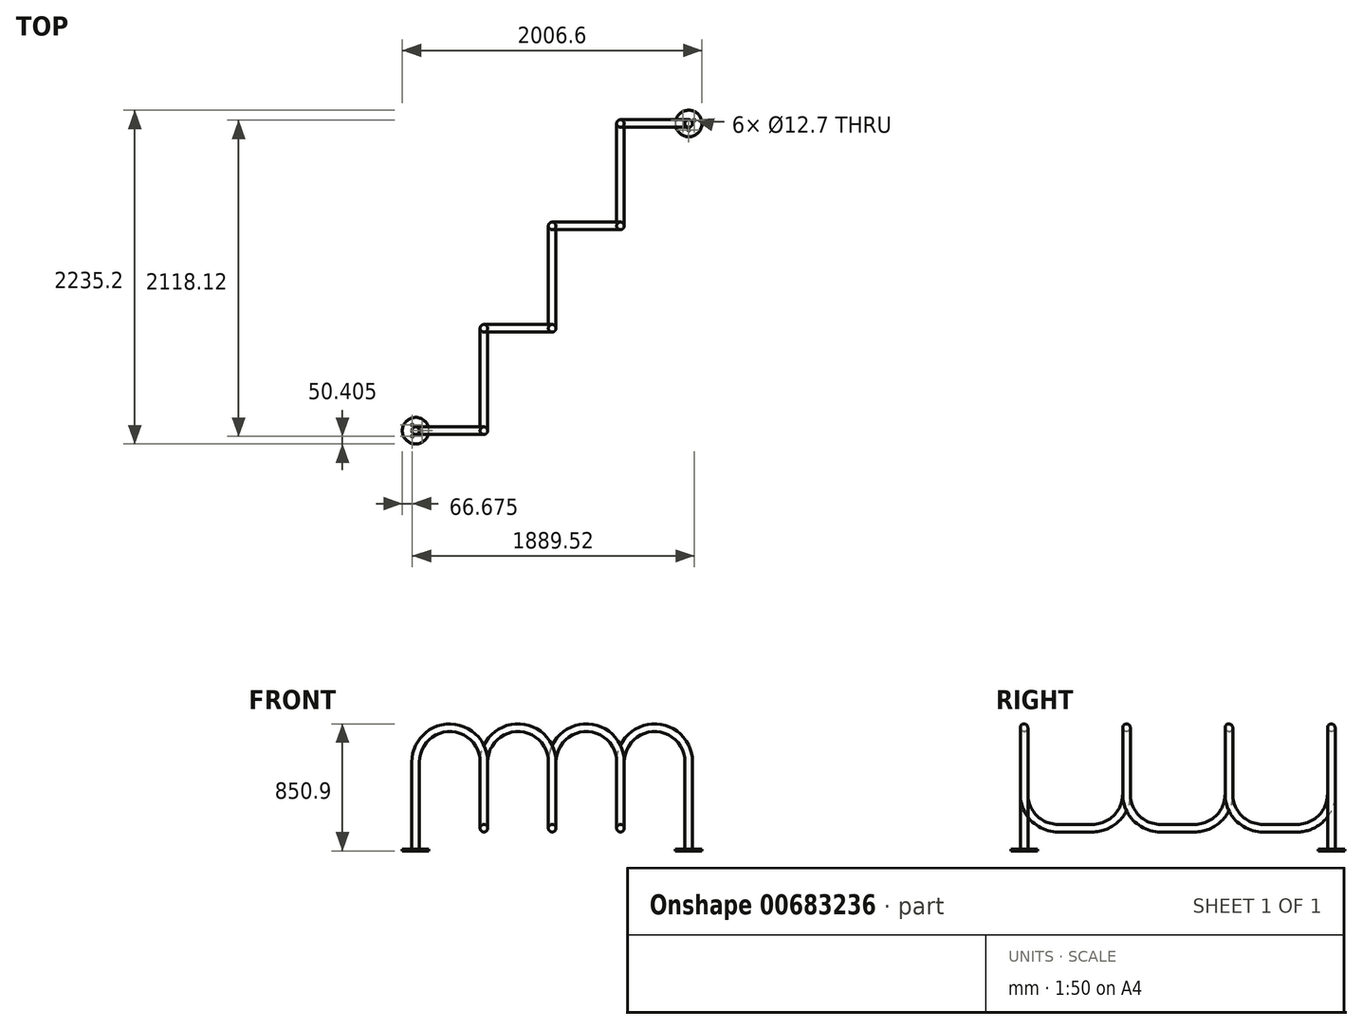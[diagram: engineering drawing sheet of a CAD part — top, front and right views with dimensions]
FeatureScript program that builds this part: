
annotation { "Feature Type Name" : "Feature", "Feature Type Description" : "" }
export const myFeature = defineFeature(function(context is Context, id is Id, definition is map)
    precondition{}
    {
        {
            var Q0;
            Q0=qCreatedBy(makeId("Front.planeOp"),FACE);
            var sketch = newSketch(context, id + "F0", { "sketchPlane" : qUnion([Q0])});
            skLineSegment(sketch, "E0", {"start": v(0, 0) * mm, "end": v(0, 596.9) * mm});
            skArc(sketch, "E1", {"start": v(457.2, 596.9) * mm, "mid": v(228.6, 825.5) * mm, "end": v(0, 596.9) * mm});
            skLineSegment(sketch, "E2", {"start": v(457.2, 596.9) * mm, "end": v(457.2, 381) * mm});
            skSolve(sketch);
        }
        {
            var Q0;
            Q0=sQuery(id+"F0.wireOp",EDGE,"E2");
            cPlane(context, id + "F1", {"entities" : qUnion([Q0]), "cplaneType" : CPlaneType.LINE_ANGLE, "offset" : 25.4 * mm, "angle" : 0 * degree, "width" : 152.4 * mm, "height" : 152.4 * mm});
        }
        {
            var Q0;
            Q0=qCreatedBy(id+"F1.planeOp",FACE);
            var sketch = newSketch(context, id + "F2", { "sketchPlane" : qUnion([Q0])});
            skLineSegment(sketch, "E3", {"start": v(-228.6, 152.4) * mm, "end": v(-457.2, 152.4) * mm});
            skLineSegment(sketch, "E4", {"start": v(-685.8, 381) * mm, "end": v(-685.8, 381) * mm});
            skLineSegment(sketch, "E5", {"start": v(-685.8, 381) * mm, "end": v(-685.8, 596.9) * mm});
            skLineSegment(sketch, "E6.0", {"start": v(0, 596.9) * mm, "end": v(0, 381) * mm});
            skArc(sketch, "E7.filletArc", {"start": v(-228.6, 152.4) * mm, "mid": v(-66.96, 219.36) * mm, "end": v(0, 381) * mm});
            skPoint(sketch, "E8.visualSharp", {"position": v(-685.8, 152.4) * mm});
            skArc(sketch, "E8.filletArc", {"start": v(-685.8, 381) * mm, "mid": v(-618.84, 219.36) * mm, "end": v(-457.2, 152.4) * mm});
            skSolve(sketch);
        }
        {
            var Q0;
            Q0=qCreatedBy(makeId("Top.planeOp"),FACE);
            var sketch = newSketch(context, id + "F3", { "sketchPlane" : qUnion([Q0])});
            skCircle(sketch, "E9", {"center": v(0, 0) * mm, "radius": 25.4 * mm});
            skSolve(sketch);
        }
        {
            var Q0;
            Q0 = qSketchRegion(id + "F3", true);
            var Q1;
            Q1=sQuery(id+"F0.wireOp",EDGE,"E0");
            var Q2;
            Q2=sQuery(id+"F0.wireOp",EDGE,"E1");
            var Q3;
            Q3=sQuery(id+"F2.wireOp",EDGE,"E6.0");
            var Q4;
            Q4=sQuery(id+"F2.wireOp",EDGE,"E7.filletArc");
            var Q5;
            Q5=sQuery(id+"F2.wireOp",EDGE,"E3");
            var Q6;
            Q6=sQuery(id+"F2.wireOp",EDGE,"E8.filletArc");
            var Q7;
            Q7=sQuery(id+"F2.wireOp",EDGE,"E5");
            sweep(context, id + "F4", {"profiles" : qUnion([Q0]), "path" : qUnion([Q1, Q2, Q3, Q4, Q5, Q6, Q7])});
        }
        {
            var Q0;
            Q0=sQuery(id+"F2.wireOp",EDGE,"E5");
            cPlane(context, id + "F5", {"entities" : qUnion([Q0]), "cplaneType" : CPlaneType.LINE_ANGLE, "offset" : 25.4 * mm, "angle" : 90 * degree, "width" : 152.4 * mm, "height" : 152.4 * mm});
        }
        {
            var Q0;
            Q0=qCreatedBy(id+"F5.planeOp",FACE);
            var sketch = newSketch(context, id + "F6", { "sketchPlane" : qUnion([Q0])});
            skArc(sketch, "E10", {"start": v(-457.2, 596.9) * mm, "mid": v(-685.8, 825.5) * mm, "end": v(-914.4, 596.9) * mm});
            skLineSegment(sketch, "E11", {"start": v(-914.4, 596.9) * mm, "end": v(-914.4, 381) * mm});
            skSolve(sketch);
        }
        {
            var Q0;
            Q0=makeQuery(id+"F4.opSweep","CAP_FACE",FACE,{"disambiguationData":[OSD([sQuery(id+"F2.wireOp",VERTEX,"E5.end"),sQuery(id+"F3.wireOp",EDGE,"E9")])],"isStart":false});
            var Q1;
            Q1=sQuery(id+"F6.wireOp",EDGE,"E10");
            var Q2;
            Q2=sQuery(id+"F6.wireOp",EDGE,"E11");
            sweep(context, id + "F7", {"operationType" : NewBodyOperationType.ADD, "profiles" : qUnion([Q0]), "path" : qUnion([Q1, Q2])});
        }
        {
            var Q0;
            Q0=sQuery(id+"F6.wireOp",EDGE,"E11");
            cPlane(context, id + "F8", {"entities" : qUnion([Q0]), "cplaneType" : CPlaneType.LINE_ANGLE, "offset" : 25.4 * mm, "angle" : 0 * degree, "width" : 152.4 * mm, "height" : 152.4 * mm});
        }
        {
            var Q0;
            Q0=qCreatedBy(id+"F8.planeOp",FACE);
            var sketch = newSketch(context, id + "F9", { "sketchPlane" : qUnion([Q0])});
            skPoint(sketch, "E12.0", {"position": v(-685.8, 381) * mm});
            skLineSegment(sketch, "E13", {"start": v(-685.8, 381) * mm, "end": v(-685.8, 381) * mm});
            skLineSegment(sketch, "E14", {"start": v(-914.4, 152.4) * mm, "end": v(-1143, 152.4) * mm});
            skLineSegment(sketch, "E15", {"start": v(-1371.6, 381) * mm, "end": v(-1371.6, 381) * mm});
            skPoint(sketch, "E16.visualSharp", {"position": v(-685.8, 152.4) * mm});
            skArc(sketch, "E16.filletArc", {"start": v(-914.4, 152.4) * mm, "mid": v(-752.76, 219.36) * mm, "end": v(-685.8, 381) * mm});
            skPoint(sketch, "E17.visualSharp", {"position": v(-1371.6, 152.4) * mm});
            skArc(sketch, "E17.filletArc", {"start": v(-1371.6, 381) * mm, "mid": v(-1304.64, 219.36) * mm, "end": v(-1143, 152.4) * mm});
            skLineSegment(sketch, "E18", {"start": v(-1371.6, 381) * mm, "end": v(-1371.6, 596.9) * mm});
            skSolve(sketch);
        }
        {
            var Q0;
            Q0=makeQuery(id+"F7.opSweep","CAP_FACE",FACE,{"disambiguationData":[OSD([sQuery(id+"F2.wireOp",VERTEX,"E5.end"),sQuery(id+"F3.wireOp",EDGE,"E9"),sQuery(id+"F6.wireOp",VERTEX,"E11.end")])],"isStart":false});
            var Q1;
            Q1=sQuery(id+"F9.wireOp",EDGE,"E16.filletArc");
            var Q2;
            Q2=sQuery(id+"F9.wireOp",EDGE,"E14");
            var Q3;
            Q3=sQuery(id+"F9.wireOp",EDGE,"E17.filletArc");
            var Q4;
            Q4=sQuery(id+"F9.wireOp",EDGE,"E18");
            sweep(context, id + "F10", {"operationType" : NewBodyOperationType.ADD, "profiles" : qUnion([Q0]), "path" : qUnion([Q1, Q2, Q3, Q4])});
        }
        {
            var Q0;
            Q0=sQuery(id+"F9.wireOp",EDGE,"E18");
            cPlane(context, id + "F11", {"entities" : qUnion([Q0]), "cplaneType" : CPlaneType.LINE_ANGLE, "offset" : 25.4 * mm, "angle" : 90 * degree, "width" : 152.4 * mm, "height" : 152.4 * mm});
        }
        {
            var Q0;
            Q0=qCreatedBy(id+"F11.planeOp",FACE);
            var sketch = newSketch(context, id + "F12", { "sketchPlane" : qUnion([Q0])});
            skArc(sketch, "E19", {"start": v(-914.4, 596.9) * mm, "mid": v(-1143, 825.5) * mm, "end": v(-1371.6, 596.9) * mm});
            skLineSegment(sketch, "E20", {"start": v(-914.4, 596.9) * mm, "end": v(-1371.6, 596.9) * mm, "construction": true});
            skLineSegment(sketch, "E21", {"start": v(-1371.6, 596.9) * mm, "end": v(-1371.6, 381) * mm});
            skSolve(sketch);
        }
        {
            var Q0;
            Q0=makeQuery(id+"F10.opSweep","CAP_FACE",FACE,{"disambiguationData":[OSD([sQuery(id+"F2.wireOp",VERTEX,"E5.end"),sQuery(id+"F3.wireOp",EDGE,"E9"),sQuery(id+"F6.wireOp",VERTEX,"E11.end"),sQuery(id+"F9.wireOp",VERTEX,"E18.end")])],"isStart":false});
            var Q1;
            Q1=sQuery(id+"F12.wireOp",EDGE,"E19");
            var Q2;
            Q2=sQuery(id+"F12.wireOp",EDGE,"E21");
            sweep(context, id + "F13", {"operationType" : NewBodyOperationType.ADD, "profiles" : qUnion([Q0]), "path" : qUnion([Q1, Q2])});
        }
        {
            var Q0;
            Q0=sQuery(id+"F12.wireOp",EDGE,"E21");
            cPlane(context, id + "F14", {"entities" : qUnion([Q0]), "cplaneType" : CPlaneType.LINE_ANGLE, "offset" : 25.4 * mm, "angle" : 0 * degree, "width" : 152.4 * mm, "height" : 152.4 * mm});
        }
        {
            var Q0;
            Q0=qCreatedBy(id+"F14.planeOp",FACE);
            var sketch = newSketch(context, id + "F15", { "sketchPlane" : qUnion([Q0])});
            skLineSegment(sketch, "E22", {"start": v(-1371.6, 381) * mm, "end": v(-1371.6, 381) * mm});
            skLineSegment(sketch, "E23", {"start": v(-1600.2, 152.4) * mm, "end": v(-1828.8, 152.4) * mm});
            skLineSegment(sketch, "E24", {"start": v(-2057.4, 381) * mm, "end": v(-2057.4, 381) * mm});
            skLineSegment(sketch, "E25", {"start": v(-2057.4, 381) * mm, "end": v(-2057.4, 596.9) * mm});
            skPoint(sketch, "E26.visualSharp", {"position": v(-1371.6, 152.4) * mm});
            skArc(sketch, "E26.filletArc", {"start": v(-1600.2, 152.4) * mm, "mid": v(-1438.56, 219.36) * mm, "end": v(-1371.6, 381) * mm});
            skPoint(sketch, "E27.visualSharp", {"position": v(-2057.4, 152.4) * mm});
            skArc(sketch, "E27.filletArc", {"start": v(-2057.4, 381) * mm, "mid": v(-1990.44, 219.36) * mm, "end": v(-1828.8, 152.4) * mm});
            skSolve(sketch);
        }
        {
            var Q0;
            Q0=makeQuery(id+"F13.opSweep","CAP_FACE",FACE,{"disambiguationData":[OSD([sQuery(id+"F2.wireOp",VERTEX,"E5.end"),sQuery(id+"F3.wireOp",EDGE,"E9"),sQuery(id+"F6.wireOp",VERTEX,"E11.end"),sQuery(id+"F9.wireOp",VERTEX,"E18.end"),sQuery(id+"F12.wireOp",VERTEX,"E21.end")])],"isStart":false});
            var Q1;
            Q1=sQuery(id+"F15.wireOp",EDGE,"E26.filletArc");
            var Q2;
            Q2=sQuery(id+"F15.wireOp",EDGE,"E23");
            var Q3;
            Q3=sQuery(id+"F15.wireOp",EDGE,"E27.filletArc");
            var Q4;
            Q4=sQuery(id+"F15.wireOp",EDGE,"E25");
            sweep(context, id + "F16", {"operationType" : NewBodyOperationType.ADD, "profiles" : qUnion([Q0]), "path" : qUnion([Q1, Q2, Q3, Q4])});
        }
        {
            var Q0;
            Q0=sQuery(id+"F15.wireOp",EDGE,"E25");
            cPlane(context, id + "F17", {"entities" : qUnion([Q0]), "cplaneType" : CPlaneType.LINE_ANGLE, "offset" : 25.4 * mm, "angle" : 90 * degree, "width" : 152.4 * mm, "height" : 152.4 * mm});
        }
        {
            var Q0;
            Q0=qCreatedBy(id+"F17.planeOp",FACE);
            var sketch = newSketch(context, id + "F18", { "sketchPlane" : qUnion([Q0])});
            skArc(sketch, "E28", {"start": v(-1371.6, 596.9) * mm, "mid": v(-1600.2, 825.5) * mm, "end": v(-1828.8, 596.9) * mm});
            skLineSegment(sketch, "E29", {"start": v(-1371.6, 596.9) * mm, "end": v(-1828.8, 596.9) * mm, "construction": true});
            skLineSegment(sketch, "E30", {"start": v(-1828.8, 596.9) * mm, "end": v(-1828.8, 0) * mm});
            skSolve(sketch);
        }
        {
            var Q0;
            Q0=makeQuery(id+"F16.opSweep","CAP_FACE",FACE,{"disambiguationData":[OSD([sQuery(id+"F2.wireOp",VERTEX,"E5.end"),sQuery(id+"F3.wireOp",EDGE,"E9"),sQuery(id+"F6.wireOp",VERTEX,"E11.end"),sQuery(id+"F9.wireOp",VERTEX,"E18.end"),sQuery(id+"F12.wireOp",VERTEX,"E21.end"),sQuery(id+"F15.wireOp",VERTEX,"E25.end")])],"isStart":false});
            var Q1;
            Q1=sQuery(id+"F18.wireOp",EDGE,"E28");
            var Q2;
            Q2=sQuery(id+"F18.wireOp",EDGE,"E30");
            sweep(context, id + "F19", {"operationType" : NewBodyOperationType.ADD, "profiles" : qUnion([Q0]), "path" : qUnion([Q1, Q2])});
        }
        {
            var Q0;
            Q0=qCreatedBy(makeId("Top.planeOp"),FACE);
            var sketch = newSketch(context, id + "F20", { "sketchPlane" : qUnion([Q0])});
            skCircle(sketch, "E31", {"center": v(0, 0) * mm, "radius": 88.9 * mm});
            skLineSegment(sketch, "E32", {"start": v(-44.45, -76.99) * mm, "end": v(0, 0) * mm, "construction": true});
            skLineSegment(sketch, "E33", {"start": v(0, 0) * mm, "end": v(-44.45, 76.99) * mm, "construction": true});
            skLineSegment(sketch, "E34", {"start": v(0, 0) * mm, "end": v(88.9, 0) * mm, "construction": true});
            skPoint(sketch, "E35", {"position": v(-22.22, -38.5) * mm});
            skPoint(sketch, "E36", {"position": v(44.45, 0) * mm});
            skPoint(sketch, "E37", {"position": v(-22.22, 38.5) * mm});
            skCircle(sketch, "E38", {"center": v(-22.22, 38.5) * mm, "radius": 6.35 * mm});
            skCircle(sketch, "E39", {"center": v(44.45, 0) * mm, "radius": 6.35 * mm});
            skCircle(sketch, "E40", {"center": v(-22.22, -38.5) * mm, "radius": 6.35 * mm});
            skSolve(sketch);
        }
        {
            var Q0;
            Q0 = qSketchRegion(id + "F20", true);
            extrude(context, id + "F21", {"entities" : qUnion([Q0]), "operationType" : NewBodyOperationType.ADD, "depth" : 12.7 * mm, "offsetDistance" : 25.4 * mm});
        }
        {
            var Q0;
            Q0=makeQuery(id+"F19.opSweep","CAP_FACE",FACE,{"disambiguationData":[OSD([sQuery(id+"F2.wireOp",VERTEX,"E5.end"),sQuery(id+"F3.wireOp",EDGE,"E9"),sQuery(id+"F6.wireOp",VERTEX,"E11.end"),sQuery(id+"F9.wireOp",VERTEX,"E18.end"),sQuery(id+"F12.wireOp",VERTEX,"E21.end"),sQuery(id+"F15.wireOp",VERTEX,"E25.end"),sQuery(id+"F18.wireOp",VERTEX,"E30.end")])],"isStart":false});
            cPlane(context, id + "F22", {"entities" : qUnion([Q0]), "cplaneType" : CPlaneType.OFFSET, "offset" : 0 * mm, "width" : 152.4 * mm, "height" : 152.4 * mm});
        }
        {
            var Q0;
            Q0=qCreatedBy(id+"F22.planeOp",FACE);
            var sketch = newSketch(context, id + "F23", { "sketchPlane" : qUnion([Q0])});
            skCircle(sketch, "E41.0", {"center": v(1828.8, -2057.4) * mm, "radius": 25.4 * mm});
            skCircle(sketch, "E42", {"center": v(1828.8, -2057.4) * mm, "radius": 88.9 * mm});
            skLineSegment(sketch, "E43", {"start": v(1828.8, -2057.4) * mm, "end": v(1905.79, -2101.85) * mm, "construction": true});
            skLineSegment(sketch, "E44", {"start": v(1828.8, -2057.4) * mm, "end": v(1828.8, -1968.5) * mm, "construction": true});
            skLineSegment(sketch, "E45", {"start": v(1828.8, -2057.4) * mm, "end": v(1751.81, -2101.85) * mm, "construction": true});
            skCircle(sketch, "E46", {"center": v(1828.8, -2012.95) * mm, "radius": 6.35 * mm});
            skCircle(sketch, "E47", {"center": v(1867.3, -2079.62) * mm, "radius": 6.35 * mm});
            skCircle(sketch, "E48", {"center": v(1790.3, -2079.62) * mm, "radius": 6.35 * mm});
            skSolve(sketch);
        }
        {
            var Q0;
            Q0 = qSketchRegion(id + "F23", true);
            extrude(context, id + "F24", {"entities" : qUnion([Q0]), "operationType" : NewBodyOperationType.ADD, "oppositeDirection" : true, "depth" : 12.7 * mm, "offsetDistance" : 25.4 * mm});
        }
    });
